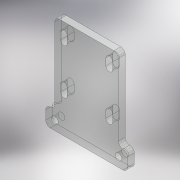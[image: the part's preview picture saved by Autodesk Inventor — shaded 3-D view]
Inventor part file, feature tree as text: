
AUTODESK INVENTOR PART (.ipt)
format: ipt  version: 2018.2 (Build 222227000, 227)  size: 188,928 bytes
history: native  units: mm
features: extrude x1, fillet x1, sketch x1
ambient origin geometry x8: Origin, YZ Plane, XZ Plane, XY Plane, X Axis, Y Axis, Z Axis, Center Point
bodies: Solid1 (feature_tree)
feature tree (3):
  extrude  "Extrusion1"  Depth=20.0mm
  fillet  "Fillet1"  Radius=3.0mm
  sketch  "Sketch1"  dims[d0=20.0mm d1=20.0mm d2=3.0mm d3=3.0mm d4=3.0mm d5=3.0mm d6=3.0mm d7=3.0mm d8=3.0mm d9=3.0mm d10=3.0mm d11=10.0mm d12=28.0mm d13=4.0mm d15=4.0mm d16=4.0mm d17=36.0mm d18=3.0mm d19=3.0mm d20=0.0mm d21=2.0mm]
